# Revit family: Urinal-Pipes-KOHLER-Exposed-K-2384T_1
name_source: partatom
category: Plumbing Fixtures
units: mm (PartAtom-declared; Revit-internal decimal feet)

## family parameters
Cut with Voids When Loaded = No
Host = Face
OmniClass Number = 23.31.25.00
OmniClass Title = Toilet and Bath Specialties
Part Type = Normal
Room Calculation Point = No
Round Connector Dimension = Use Diameter
Shared = No

## types (1)
- CP-Polished Chrome
    ADA Compliant = No
    Assembly Code = D2010200
    CW Connection = Yes
    Cold Water Inlet = Cold Water Inlet
    Cold Water Outlet = Cold Water Outlet
    Date Modified = 04/13/2023
    Default Elevation = 36"
    Description = Urinal Sensor Unbent Pipe
    Finish = Kohler-Metal-CP-Polished_Chrome
    Flow Rate = 0 GPM
    Flush Rate- GPF = GPF
    Flush Rate- LPF = LPF
    HW Connection = No
    Height = 10 11/16"
    Hot Water Inlet = Hot Water Inlet
    Length = 2 5/16"
    Manufacturer = Kohler Co.
    Master Format 2014 = 22 41 13.16
    Master Format 2014 Name = Residential Urinals
    Material = Premium Metal Construction
    Model = K-2348T-NA
    Pressure = 0.00 psi
    Product Name = Exposed
    Rough-In = 0"
    Type = 1
    URL = http://www.kohler.com.cn
    Vent Connection = No
    Waste Connection = No
    Waste Water Outlet = Waste Water Outlet
    WaterSense Certified = No
    Width = 2 5/16"

## geometry (parser evidence)
native form markers: Sweep x5
no freeform markers — native parametric forms only
